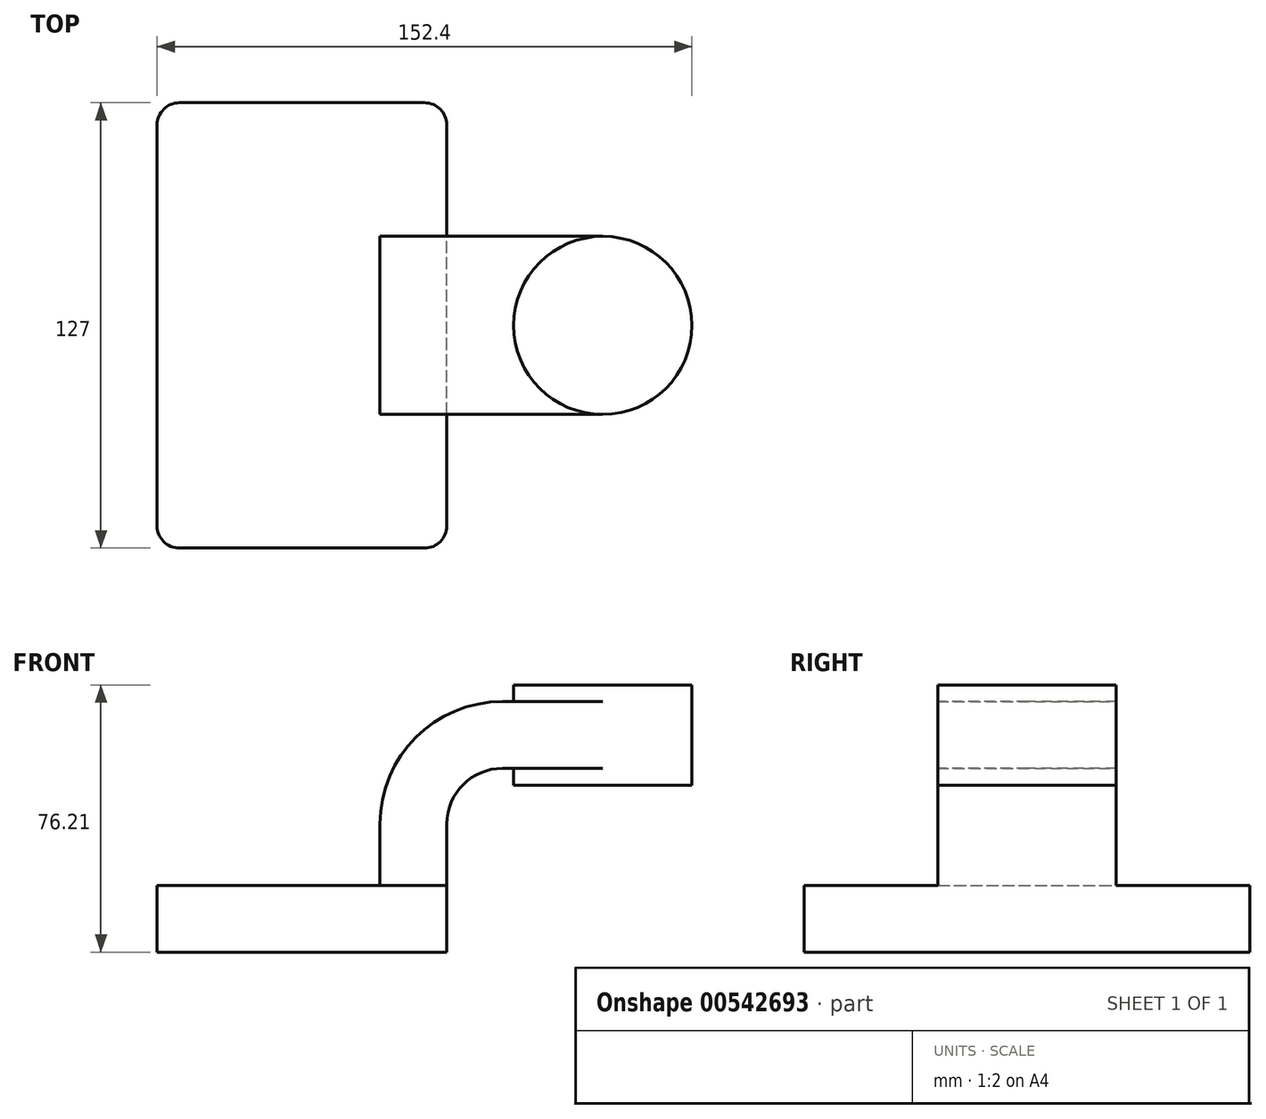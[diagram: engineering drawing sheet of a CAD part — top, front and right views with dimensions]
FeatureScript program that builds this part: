
annotation { "Feature Type Name" : "Feature", "Feature Type Description" : "" }
export const myFeature = defineFeature(function(context is Context, id is Id, definition is map)
    precondition{}
    {
        {
            var Q0;
            Q0=qCreatedBy(makeId("Front.planeOp"),FACE);
            var sketch = newSketch(context, id + "F0", { "sketchPlane" : qUnion([Q0])});
            skLineSegment(sketch, "E0.bottom", {"start": v(41.28, 9.53) * mm, "end": v(-41.28, 9.53) * mm});
            skLineSegment(sketch, "E0.top", {"start": v(41.28, -9.52) * mm, "end": v(-41.28, -9.52) * mm});
            skLineSegment(sketch, "E0.left", {"start": v(41.28, 9.53) * mm, "end": v(41.28, -9.52) * mm});
            skLineSegment(sketch, "E0.right", {"start": v(-41.28, 9.53) * mm, "end": v(-41.28, -9.52) * mm});
            skPoint(sketch, "E0.middle", {"position": v(0, 0) * mm});
            skLineSegment(sketch, "E1.bottom", {"start": v(60.32, 66.68) * mm, "end": v(111.12, 66.68) * mm});
            skLineSegment(sketch, "E1.top", {"start": v(60.33, 38.1) * mm, "end": v(111.12, 38.1) * mm});
            skLineSegment(sketch, "E1.left", {"start": v(60.32, 66.67) * mm, "end": v(60.33, 38.1) * mm});
            skLineSegment(sketch, "E1.right", {"start": v(111.12, 66.67) * mm, "end": v(111.12, 38.1) * mm});
            skPoint(sketch, "E1.middle", {"position": v(85.72, 52.39) * mm});
            skLineSegment(sketch, "E2", {"start": v(41.28, 9.53) * mm, "end": v(41.28, 27) * mm});
            skArc(sketch, "E3", {"start": v(41.27, 27) * mm, "mid": v(45.92, 38.23) * mm, "end": v(57.15, 42.88) * mm});
            skPoint(sketch, "E4.endSnap0", {"position": v(45.92, 38.23) * mm});
            skLineSegment(sketch, "E5", {"start": v(57.15, 42.88) * mm, "end": v(85.73, 42.88) * mm});
            skLineSegment(sketch, "E6.0", {"start": v(57.15, 61.93) * mm, "end": v(85.73, 61.93) * mm});
            skArc(sketch, "E6.1", {"start": v(22.22, 27) * mm, "mid": v(32.45, 51.7) * mm, "end": v(57.15, 61.93) * mm});
            skLineSegment(sketch, "E6.2", {"start": v(22.22, 9.53) * mm, "end": v(22.22, 27) * mm});
            skLineSegment(sketch, "E7", {"start": v(85.72, 38.1) * mm, "end": v(85.72, 66.68) * mm});
            skFitSpline(sketch, "E8", {"points": [v(-41.28, 9.53) * mm, v(57.15, 61.93) * mm], "startDerivative": vector(0.51, 60.85) * mm, "endDerivative": vector(157.33, -13.78) * mm});
            skSolve(sketch);
        }
        {
            var Q0;
            Q0=makeQuery(id+"F0.imprint","IMPRINT",FACE,{"disambiguationData":[TD([[makeQuery(id+"F0.imprint","IMPRINT",EDGE,{"derivedFrom":sQuery(id+"F0.wireOp",EDGE,"E0.top")}),-1.0]])]});
            extrude(context, id + "F1", {"entities" : qUnion([Q0]), "endBound" : BoundingType.SYMMETRIC, "depth" : 127 * mm, "offsetDistance" : 25.4 * mm});
        }
        {
            var Q0;
            {var subQ1=sQuery(id+"F0.wireOp",EDGE,"E2");Q0=makeQuery(id+"F0.imprint","IMPRINT",FACE,{"disambiguationData":[TD([[makeQuery(id+"F0.imprint","IMPRINT",EDGE,{"derivedFrom":subQ1}),1.0]])]});}
            var Q1;
            {var subQ0=sQuery(id+"F0.wireOp",EDGE,"E6.0");var subQ1=sQuery(id+"F0.wireOp",EDGE,"E1.left");var subQ2=makeQuery(id+"F0.imprint","INTERSECT",VERTEX,{"derivedFrom":[subQ1,subQ0]});Q1=makeQuery(id+"F0.imprint","IMPRINT",FACE,{"disambiguationData":[TD([[makeQuery(id+"F0.imprint","IMPRINT",EDGE,{"disambiguationData":[TD([[subQ2,-1.0]])],"derivedFrom":subQ1}),1.0]])]});}
            extrude(context, id + "F2", {"entities" : qUnion([Q0, Q1]), "operationType" : NewBodyOperationType.ADD, "endBound" : BoundingType.SYMMETRIC, "depth" : 50.8 * mm, "offsetDistance" : 25.4 * mm});
        }
        {
            var Q0;
            Q0=makeQuery(id+"F0.imprint","IMPRINT",FACE,{"disambiguationData":[TD([[makeQuery(id+"F0.imprint","IMPRINT",EDGE,{"derivedFrom":sQuery(id+"F0.wireOp",EDGE,"E6.1")}),1.0]])]});
            extrude(context, id + "F3", {"entities" : qUnion([Q0]), "operationType" : NewBodyOperationType.ADD, "endBound" : BoundingType.SYMMETRIC, "depth" : 15.88 * mm, "offsetDistance" : 25.4 * mm});
        }
        {
            var Q0;
            {var subQ0=sQuery(id+"F0.wireOp",EDGE,"E1.right");Q0=makeQuery(id+"F0.imprint","IMPRINT",FACE,{"disambiguationData":[TD([[makeQuery(id+"F0.imprint","IMPRINT",EDGE,{"derivedFrom":subQ0}),-1.0]])]});}
            var Q1;
            Q1=sQuery(id+"F0.wireOp",EDGE,"E7");
            revolve(context, id + "F4", {"operationType" : NewBodyOperationType.ADD, "entities" : qUnion([Q0]), "axis" : qUnion([Q1]), "revolveType" : RevolveType.FULL});
        }
        {
            var Q0;
            Q0=makeQuery(id+"F1.opExtrude","CAP_EDGE",EDGE,{"disambiguationData":[OSD([sQuery(id+"F0.wireOp",EDGE,"E0.left")])],"isStart":false});
            var Q1;
            Q1=makeQuery(id+"F1.opExtrude","CAP_EDGE",EDGE,{"disambiguationData":[OSD([sQuery(id+"F0.wireOp",EDGE,"E0.right")])],"isStart":false});
            var Q2;
            Q2=makeQuery(id+"F1.opExtrude","CAP_EDGE",EDGE,{"disambiguationData":[OSD([sQuery(id+"F0.wireOp",EDGE,"E0.left")])],"isStart":true});
            var Q3;
            Q3=makeQuery(id+"F1.opExtrude","CAP_EDGE",EDGE,{"disambiguationData":[OSD([sQuery(id+"F0.wireOp",EDGE,"E0.right")])],"isStart":true});
            fillet(context, id + "F5", {"entities" : qUnion([Q0, Q1, Q2, Q3]), "radius" : 6.35 * mm, "tangentPropagation" : true, "allowEdgeOverflow" : false});
        }
    });
